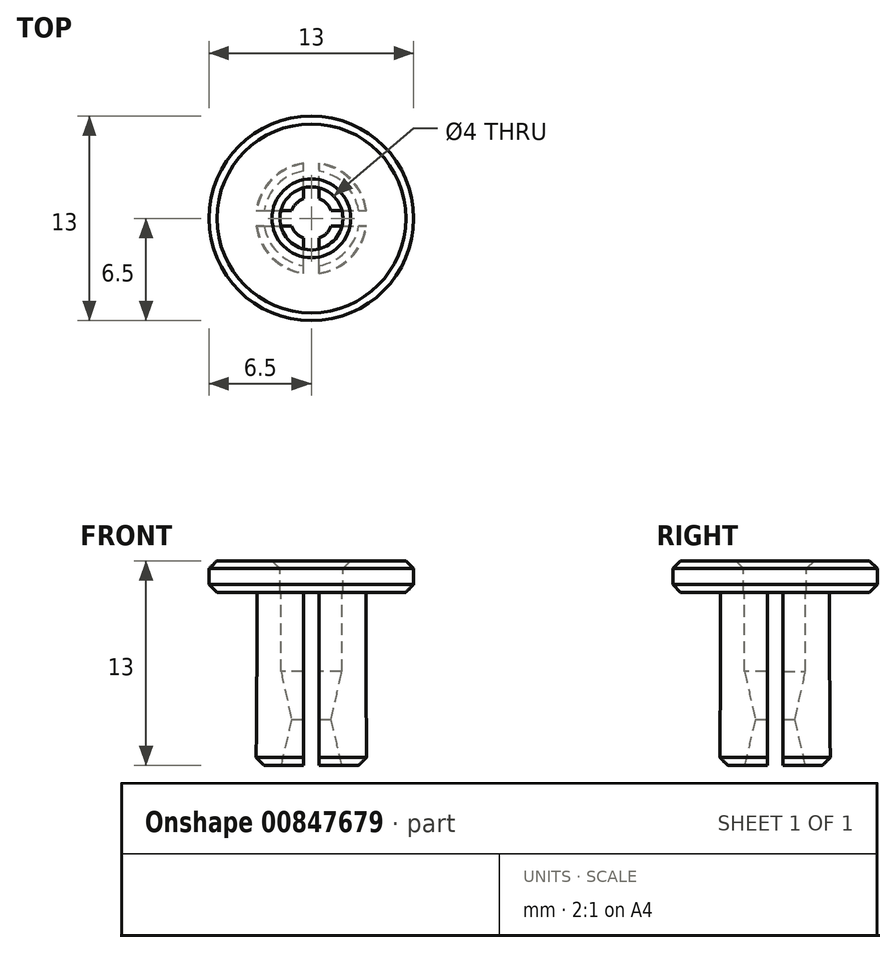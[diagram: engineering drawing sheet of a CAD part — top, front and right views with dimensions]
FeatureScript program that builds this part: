
annotation { "Feature Type Name" : "Feature", "Feature Type Description" : "" }
export const myFeature = defineFeature(function(context is Context, id is Id, definition is map)
    precondition{}
    {
        {
            var Q0;
            Q0=qCreatedBy(makeId("Front.planeOp"),FACE);
            var sketch = newSketch(context, id + "F0", { "sketchPlane" : qUnion([Q0])});
            skLineSegment(sketch, "E0", {"start": v(0, -13) * mm, "end": v(-3.54, -13) * mm});
            skLineSegment(sketch, "E1", {"start": v(-3.54, -13) * mm, "end": v(-3.5, -7) * mm});
            skLineSegment(sketch, "E2", {"start": v(-3.5, -7) * mm, "end": v(-3.5, -2) * mm});
            skLineSegment(sketch, "E3", {"start": v(-3.5, -2) * mm, "end": v(-6.5, -2) * mm});
            skLineSegment(sketch, "E4", {"start": v(-6.5, -2) * mm, "end": v(-6.5, 0) * mm});
            skLineSegment(sketch, "E5", {"start": v(-6.5, 0) * mm, "end": v(0, 0) * mm});
            skPoint(sketch, "E6", {"position": v(-2, 2.21) * mm});
            skLineSegment(sketch, "E7", {"start": v(-2, 0) * mm, "end": v(-2, -7.02) * mm});
            skLineSegment(sketch, "E8", {"start": v(-4.61, -15.25) * mm, "end": v(3.45, -15.25) * mm});
            skPoint(sketch, "E9.orphan", {"position": v(0, -15.25) * mm});
            skPoint(sketch, "E10", {"position": v(-2, -7.02) * mm});
            skLineSegment(sketch, "E11", {"start": v(-2, -7.02) * mm, "end": v(-1.35, -10.07) * mm});
            skLineSegment(sketch, "E12", {"start": v(-1.35, -10.07) * mm, "end": v(-2, -13) * mm});
            skLineSegment(sketch, "E13", {"start": v(0, 8.2) * mm, "end": v(0, -21.82) * mm, "construction": true});
            skSolve(sketch);
        }
        {
            var Q0;
            {var subQ0=sQuery(id+"F0.wireOp",EDGE,"E1");Q0=makeQuery(id+"F0.imprint","IMPRINT",FACE,{"disambiguationData":[TD([[makeQuery(id+"F0.imprint","IMPRINT",EDGE,{"derivedFrom":subQ0}),-1.0]])]});}
            var Q1;
            Q1=sQuery(id+"F0.wireOp",EDGE,"E13");
            revolve(context, id + "F1", {"surfaceOperationType" : NewSurfaceOperationType.NEW, "entities" : qUnion([Q0]), "axis" : qUnion([Q1]), "revolveType" : RevolveType.FULL});
        }
        {
            var Q0;
            Q0=makeQuery(id+"F1.opRevolve","SWEPT_FACE",FACE,{"disambiguationData":[OSD([sQuery(id+"F0.wireOp",EDGE,"E0")])]});
            var sketch = newSketch(context, id + "F2", { "sketchPlane" : qUnion([Q0])});
            skLineSegment(sketch, "E14.bottom", {"start": v(-0.5, 3.84) * mm, "end": v(0.5, 3.84) * mm});
            skLineSegment(sketch, "E14.top", {"start": v(-0.5, -4.2) * mm, "end": v(0.5, -4.2) * mm});
            skLineSegment(sketch, "E14.left", {"start": v(-0.5, 3.84) * mm, "end": v(-0.5, -4.2) * mm});
            skLineSegment(sketch, "E14.right", {"start": v(0.5, 3.84) * mm, "end": v(0.5, -4.2) * mm});
            skLineSegment(sketch, "E15.bottom", {"start": v(-4.4, 0.5) * mm, "end": v(4.5, 0.5) * mm});
            skLineSegment(sketch, "E15.top", {"start": v(-4.4, -0.5) * mm, "end": v(4.5, -0.5) * mm});
            skLineSegment(sketch, "E15.left", {"start": v(-4.4, 0.5) * mm, "end": v(-4.4, -0.5) * mm});
            skLineSegment(sketch, "E15.right", {"start": v(4.5, 0.5) * mm, "end": v(4.5, -0.5) * mm});
            skSolve(sketch);
        }
        {
            var Q0;
            {var subQ0=sQuery(id+"F2.wireOp",EDGE,"E14.left");var subQ1=sQuery(id+"F0.wireOp",EDGE,"E0");var subQ2=makeQuery(id+"F1.opRevolve","SWEPT_EDGE",EDGE,{"disambiguationData":[OSD([subQ1,sQuery(id+"F0.wireOp",EDGE,"E1")])]});var subQ3=makeQuery(id+"F2.imprint","INTERSECT",VERTEX,{"disambiguationData":[OD(0.0)],"derivedFrom":[subQ2,subQ0]});Q0=makeQuery(id+"F2.imprint","IMPRINT",FACE,{"disambiguationData":[TD([[makeQuery(id+"F2.imprint","IMPRINT",EDGE,{"disambiguationData":[TD([[subQ3,-1.0]])],"derivedFrom":subQ0}),1.0]])]});}
            var Q1;
            {var subQ0=sQuery(id+"F2.wireOp",EDGE,"E14.bottom");Q1=makeQuery(id+"F2.imprint","IMPRINT",FACE,{"disambiguationData":[TD([[makeQuery(id+"F2.imprint","IMPRINT",EDGE,{"derivedFrom":subQ0}),-1.0]])]});}
            var Q2;
            {var subQ0=sQuery(id+"F2.wireOp",EDGE,"E15.right");Q2=makeQuery(id+"F2.imprint","IMPRINT",FACE,{"disambiguationData":[TD([[makeQuery(id+"F2.imprint","IMPRINT",EDGE,{"derivedFrom":subQ0}),-1.0]])]});}
            var Q3;
            {var subQ0=sQuery(id+"F2.wireOp",EDGE,"E15.bottom");var subQ1=sQuery(id+"F0.wireOp",EDGE,"E0");var subQ2=makeQuery(id+"F1.opRevolve","SWEPT_EDGE",EDGE,{"disambiguationData":[OSD([subQ1,sQuery(id+"F0.wireOp",EDGE,"E1")])]});var subQ3=makeQuery(id+"F2.imprint","INTERSECT",VERTEX,{"disambiguationData":[OD(1.0)],"derivedFrom":[subQ2,subQ0]});Q3=makeQuery(id+"F2.imprint","IMPRINT",FACE,{"disambiguationData":[TD([[makeQuery(id+"F2.imprint","IMPRINT",EDGE,{"disambiguationData":[TD([[subQ3,1.0]])],"derivedFrom":subQ0}),-1.0]])]});}
            var Q4;
            {var subQ0=sQuery(id+"F2.wireOp",EDGE,"E14.left");var subQ1=sQuery(id+"F0.wireOp",EDGE,"E0");var subQ2=makeQuery(id+"F1.opRevolve","SWEPT_EDGE",EDGE,{"disambiguationData":[OSD([subQ1,sQuery(id+"F0.wireOp",EDGE,"E1")])]});var subQ3=makeQuery(id+"F2.imprint","INTERSECT",VERTEX,{"disambiguationData":[OD(1.0)],"derivedFrom":[subQ2,subQ0]});Q4=makeQuery(id+"F2.imprint","IMPRINT",FACE,{"disambiguationData":[TD([[makeQuery(id+"F2.imprint","IMPRINT",EDGE,{"disambiguationData":[TD([[subQ3,1.0]])],"derivedFrom":subQ0}),1.0]])]});}
            var Q5;
            {var subQ0=sQuery(id+"F2.wireOp",EDGE,"E15.bottom");var subQ1=sQuery(id+"F0.wireOp",EDGE,"E0");var subQ2=makeQuery(id+"F1.opRevolve","SWEPT_EDGE",EDGE,{"disambiguationData":[OSD([subQ1,sQuery(id+"F0.wireOp",EDGE,"E1")])]});var subQ3=makeQuery(id+"F2.imprint","INTERSECT",VERTEX,{"disambiguationData":[OD(0.0)],"derivedFrom":[subQ2,subQ0]});Q5=makeQuery(id+"F2.imprint","IMPRINT",FACE,{"disambiguationData":[TD([[makeQuery(id+"F2.imprint","IMPRINT",EDGE,{"disambiguationData":[TD([[subQ3,-1.0]])],"derivedFrom":subQ0}),-1.0]])]});}
            var Q6;
            {var subQ0=sQuery(id+"F2.wireOp",EDGE,"E15.bottom");var subQ1=sQuery(id+"F2.wireOp",EDGE,"E14.left");var subQ2=makeQuery(id+"F2.imprint","INTERSECT",VERTEX,{"derivedFrom":[subQ1,subQ0]});Q6=makeQuery(id+"F2.imprint","IMPRINT",FACE,{"disambiguationData":[TD([[makeQuery(id+"F2.imprint","IMPRINT",EDGE,{"disambiguationData":[TD([[subQ2,-1.0]])],"derivedFrom":subQ1}),-1.0]])]});}
            var Q7;
            {var subQ0=sQuery(id+"F2.wireOp",EDGE,"E15.bottom");var subQ1=sQuery(id+"F2.wireOp",EDGE,"E14.left");var subQ2=makeQuery(id+"F2.imprint","INTERSECT",VERTEX,{"derivedFrom":[subQ1,subQ0]});Q7=makeQuery(id+"F2.imprint","IMPRINT",FACE,{"disambiguationData":[TD([[makeQuery(id+"F2.imprint","IMPRINT",EDGE,{"disambiguationData":[TD([[subQ2,-1.0]])],"derivedFrom":subQ0}),1.0]])]});}
            var Q8;
            {var subQ0=sQuery(id+"F2.wireOp",EDGE,"E15.top");var subQ1=sQuery(id+"F2.wireOp",EDGE,"E14.left");var subQ2=makeQuery(id+"F2.imprint","INTERSECT",VERTEX,{"derivedFrom":[subQ1,subQ0]});Q8=makeQuery(id+"F2.imprint","IMPRINT",FACE,{"disambiguationData":[TD([[makeQuery(id+"F2.imprint","IMPRINT",EDGE,{"disambiguationData":[TD([[subQ2,-1.0]])],"derivedFrom":subQ0}),-1.0]])]});}
            var Q9;
            {var subQ0=sQuery(id+"F2.wireOp",EDGE,"E15.bottom");var subQ1=sQuery(id+"F2.wireOp",EDGE,"E14.right");var subQ2=makeQuery(id+"F2.imprint","INTERSECT",VERTEX,{"derivedFrom":[subQ1,subQ0]});Q9=makeQuery(id+"F2.imprint","IMPRINT",FACE,{"disambiguationData":[TD([[makeQuery(id+"F2.imprint","IMPRINT",EDGE,{"disambiguationData":[TD([[subQ2,-1.0]])],"derivedFrom":subQ1}),1.0]])]});}
            var Q10;
            {var subQ0=sQuery(id+"F2.wireOp",EDGE,"E15.left");Q10=makeQuery(id+"F2.imprint","IMPRINT",FACE,{"disambiguationData":[TD([[makeQuery(id+"F2.imprint","IMPRINT",EDGE,{"derivedFrom":subQ0}),1.0]])]});}
            var Q11;
            {var subQ0=sQuery(id+"F2.wireOp",EDGE,"E14.top");Q11=makeQuery(id+"F2.imprint","IMPRINT",FACE,{"disambiguationData":[TD([[makeQuery(id+"F2.imprint","IMPRINT",EDGE,{"derivedFrom":subQ0}),1.0]])]});}
            extrude(context, id + "F3", {"entities" : qUnion([Q0, Q1, Q2, Q3, Q4, Q5, Q6, Q7, Q8, Q9, Q10, Q11]), "operationType" : NewBodyOperationType.REMOVE, "oppositeDirection" : true, "depth" : 11 * mm, "offsetDistance" : 25 * mm});
        }
        {
            var Q0;
            {var subQ0=sQuery(id+"F0.wireOp",EDGE,"E0");var subQ1=sQuery(id+"F0.wireOp",EDGE,"E1");var subQ2=sQuery(id+"F2.wireOp",EDGE,"E15.bottom");var subQ3=sQuery(id+"F2.wireOp",EDGE,"E14.left");var subQ4=makeQuery(id+"F2.imprint","INTERSECT",VERTEX,{"derivedFrom":[subQ3,subQ2]});var subQ7=makeQuery(id+"F1.opRevolve","SWEPT_EDGE",EDGE,{"disambiguationData":[OSD([subQ0,subQ1])]});var subQ8=makeQuery(id+"F2.imprint","INTERSECT",VERTEX,{"disambiguationData":[OD(0.0)],"derivedFrom":[subQ7,subQ3]});Q0=makeQuery(id+"F3.boolean.opBoolean","SPLIT",EDGE,{"disambiguationData":[TD([makeQuery(id+"F3.opExtrude","SWEPT_FACE",FACE,{"disambiguationData":[OSD([subQ3]),TDD([makeQuery(id+"F2.imprint","IMPRINT",EDGE,{"disambiguationData":[TD([[makeQuery(id+"F2.imprint","INTERSECT",VERTEX,{"derivedFrom":[sQuery(id+"F2.wireOp",EDGE,"E14.bottom"),subQ3]}),-1.0]])],"derivedFrom":subQ3}),makeQuery(id+"F2.imprint","IMPRINT",EDGE,{"disambiguationData":[TD([[subQ8,-1.0]])],"derivedFrom":subQ3}),makeQuery(id+"F2.imprint","IMPRINT",EDGE,{"disambiguationData":[TD([[subQ4,1.0]])],"derivedFrom":subQ3})])]})])],"derivedFrom":subQ7});}
            var Q1;
            {var subQ0=sQuery(id+"F0.wireOp",EDGE,"E0");var subQ1=sQuery(id+"F0.wireOp",EDGE,"E1");var subQ2=sQuery(id+"F2.wireOp",EDGE,"E14.left");var subQ3=makeQuery(id+"F1.opRevolve","SWEPT_EDGE",EDGE,{"disambiguationData":[OSD([subQ0,subQ1])]});var subQ4=makeQuery(id+"F2.imprint","INTERSECT",VERTEX,{"disambiguationData":[OD(1.0)],"derivedFrom":[subQ3,subQ2]});var subQ7=sQuery(id+"F2.wireOp",EDGE,"E15.top");var subQ8=makeQuery(id+"F2.imprint","INTERSECT",VERTEX,{"derivedFrom":[subQ2,subQ7]});Q1=makeQuery(id+"F3.boolean.opBoolean","SPLIT",EDGE,{"disambiguationData":[TD([makeQuery(id+"F3.opExtrude","SWEPT_FACE",FACE,{"disambiguationData":[OSD([subQ2]),TDD([makeQuery(id+"F2.imprint","IMPRINT",EDGE,{"disambiguationData":[TD([[subQ8,-1.0]])],"derivedFrom":subQ2}),makeQuery(id+"F2.imprint","IMPRINT",EDGE,{"disambiguationData":[TD([[subQ4,1.0]])],"derivedFrom":subQ2}),makeQuery(id+"F2.imprint","IMPRINT",EDGE,{"disambiguationData":[TD([[makeQuery(id+"F2.imprint","INTERSECT",VERTEX,{"derivedFrom":[sQuery(id+"F2.wireOp",EDGE,"E14.top"),subQ2]}),1.0]])],"derivedFrom":subQ2})])]})])],"derivedFrom":subQ3});}
            var Q2;
            {var subQ0=sQuery(id+"F0.wireOp",EDGE,"E0");var subQ1=sQuery(id+"F0.wireOp",EDGE,"E1");var subQ2=sQuery(id+"F2.wireOp",EDGE,"E14.right");var subQ3=makeQuery(id+"F1.opRevolve","SWEPT_EDGE",EDGE,{"disambiguationData":[OSD([subQ0,subQ1])]});var subQ4=makeQuery(id+"F2.imprint","INTERSECT",VERTEX,{"disambiguationData":[OD(1.0)],"derivedFrom":[subQ3,subQ2]});var subQ7=sQuery(id+"F2.wireOp",EDGE,"E15.top");var subQ8=makeQuery(id+"F2.imprint","INTERSECT",VERTEX,{"derivedFrom":[subQ2,subQ7]});Q2=makeQuery(id+"F3.boolean.opBoolean","SPLIT",EDGE,{"disambiguationData":[TD([makeQuery(id+"F3.opExtrude","SWEPT_FACE",FACE,{"disambiguationData":[OSD([subQ2]),TDD([makeQuery(id+"F2.imprint","IMPRINT",EDGE,{"disambiguationData":[TD([[subQ8,-1.0]])],"derivedFrom":subQ2}),makeQuery(id+"F2.imprint","IMPRINT",EDGE,{"disambiguationData":[TD([[subQ4,1.0]])],"derivedFrom":subQ2}),makeQuery(id+"F2.imprint","IMPRINT",EDGE,{"disambiguationData":[TD([[makeQuery(id+"F2.imprint","INTERSECT",VERTEX,{"derivedFrom":[sQuery(id+"F2.wireOp",EDGE,"E14.top"),subQ2]}),1.0]])],"derivedFrom":subQ2})])]})])],"derivedFrom":subQ3});}
            var Q3;
            {var subQ0=sQuery(id+"F0.wireOp",EDGE,"E0");var subQ1=sQuery(id+"F0.wireOp",EDGE,"E1");var subQ2=sQuery(id+"F2.wireOp",EDGE,"E15.bottom");var subQ3=makeQuery(id+"F1.opRevolve","SWEPT_EDGE",EDGE,{"disambiguationData":[OSD([subQ0,subQ1])]});var subQ7=sQuery(id+"F2.wireOp",EDGE,"E14.right");var subQ8=makeQuery(id+"F2.imprint","INTERSECT",VERTEX,{"derivedFrom":[subQ7,subQ2]});var subQ10=makeQuery(id+"F2.imprint","INTERSECT",VERTEX,{"disambiguationData":[OD(0.0)],"derivedFrom":[subQ3,subQ7]});Q3=makeQuery(id+"F3.boolean.opBoolean","SPLIT",EDGE,{"disambiguationData":[TD([makeQuery(id+"F3.opExtrude","SWEPT_FACE",FACE,{"disambiguationData":[OSD([subQ7]),TDD([makeQuery(id+"F2.imprint","IMPRINT",EDGE,{"disambiguationData":[TD([[makeQuery(id+"F2.imprint","INTERSECT",VERTEX,{"derivedFrom":[sQuery(id+"F2.wireOp",EDGE,"E14.bottom"),subQ7]}),-1.0]])],"derivedFrom":subQ7}),makeQuery(id+"F2.imprint","IMPRINT",EDGE,{"disambiguationData":[TD([[subQ10,-1.0]])],"derivedFrom":subQ7}),makeQuery(id+"F2.imprint","IMPRINT",EDGE,{"disambiguationData":[TD([[subQ8,1.0]])],"derivedFrom":subQ7})])]})])],"derivedFrom":subQ3});}
            var Q4;
            Q4=makeQuery(id+"F1.opRevolve","SWEPT_EDGE",EDGE,{"disambiguationData":[OSD([sQuery(id+"F0.wireOp",EDGE,"E4"),sQuery(id+"F0.wireOp",EDGE,"E5")])]});
            var Q5;
            Q5=makeQuery(id+"F1.opRevolve","SWEPT_EDGE",EDGE,{"disambiguationData":[OSD([sQuery(id+"F0.wireOp",EDGE,"E3"),sQuery(id+"F0.wireOp",EDGE,"E4")])]});
            var Q6;
            Q6=makeQuery(id+"F1.opRevolve","SWEPT_EDGE",EDGE,{"disambiguationData":[OSD([sQuery(id+"F0.wireOp",EDGE,"E5"),sQuery(id+"F0.wireOp",EDGE,"E7")])]});
            chamfer(context, id + "F4", {"entities" : qUnion([Q0, Q1, Q2, Q3, Q4, Q5, Q6]), "width" : .5 * mm, "tangentPropagation" : true});
        }
    });
